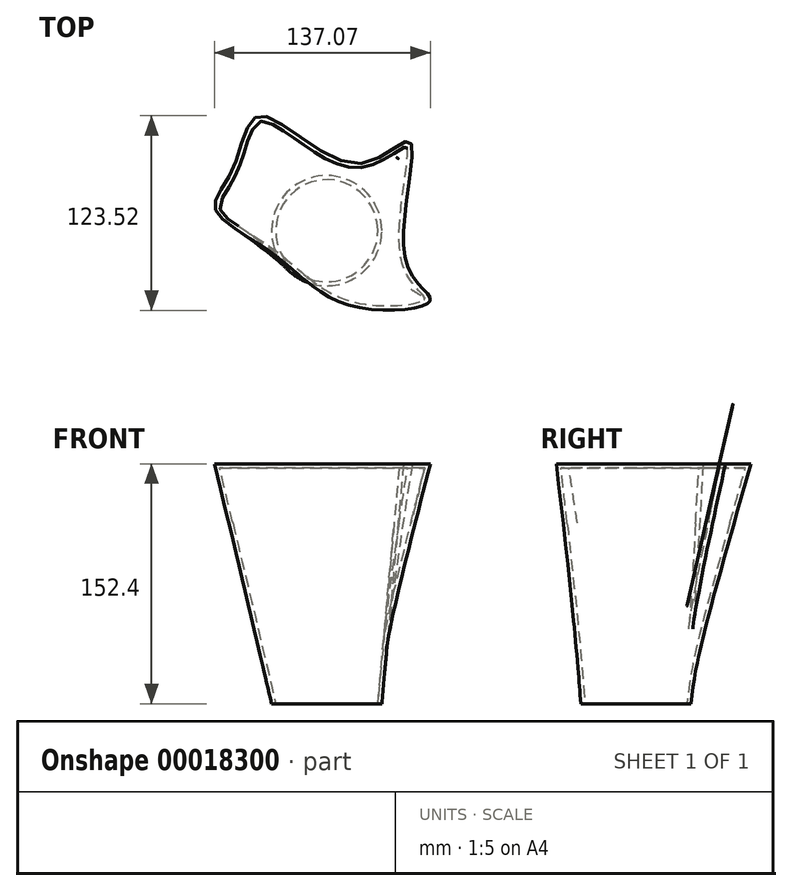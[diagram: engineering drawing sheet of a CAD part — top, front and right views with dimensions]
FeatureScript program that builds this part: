
annotation { "Feature Type Name" : "Feature", "Feature Type Description" : "" }
export const myFeature = defineFeature(function(context is Context, id is Id, definition is map)
    precondition{}
    {
        {
            var Q0;
            Q0=qCreatedBy(makeId("Top.planeOp"),FACE);
            var sketch = newSketch(context, id + "F0", { "sketchPlane" : qUnion([Q0])});
            skCircle(sketch, "E0", {"center": v(0, 0) * mm, "radius": 35.01 * mm});
            skSolve(sketch);
        }
        {
            var Q0;
            Q0=makeQuery(id+"F0.imprint","IMPRINT",FACE,{"disambiguationData":[TD([[makeQuery(id+"F0.imprint","IMPRINT",EDGE,{"derivedFrom":sQuery(id+"F0.wireOp",EDGE,"E0")}),1.0]])]});
            cPlane(context, id + "F1", {"entities" : qUnion([Q0]), "cplaneType" : CPlaneType.OFFSET, "offset" : 152.4 * mm, "width" : 152.4 * mm, "height" : 152.4 * mm});
        }
        {
            var Q0;
            Q0=qCreatedBy(id+"F1.planeOp",FACE);
            var sketch = newSketch(context, id + "F2", { "sketchPlane" : qUnion([Q0])});
            skFitSpline(sketch, "E1", {"points": [v(-59.58, 39.13) * mm, v(-42.4, 72.94) * mm, v(19.08, 42.61) * mm, v(53.06, 56.4) * mm, v(50.65, -20.13) * mm, v(65.68, -44.65) * mm, v(15.92, -47.75) * mm, v(-36.1, -13.13) * mm, v(-70.95, 13.93) * mm, v(-59.58, 39.13) * mm]});
            skSolve(sketch);
        }
        {
            var Q0;
            Q0=makeQuery(id+"F0.imprint","IMPRINT",FACE,{"disambiguationData":[TD([[makeQuery(id+"F0.imprint","IMPRINT",EDGE,{"derivedFrom":sQuery(id+"F0.wireOp",EDGE,"E0")}),1.0]])]});
            var Q1;
            Q1=makeQuery(id+"F2.imprint","IMPRINT",FACE,{"disambiguationData":[TD([[makeQuery(id+"F2.imprint","IMPRINT",EDGE,{"derivedFrom":sQuery(id+"F2.wireOp",EDGE,"E1")}),-1.0]])]});
            loft(context, id + "F3", {"sheetProfilesArray" : [{ "sheetProfileEntities" : qUnion([Q0]) }, { "sheetProfileEntities" : qUnion([Q1]) }]});
        }
        {
            var Q0;
            Q0=makeQuery(id+"F3.opLoft","CAP_FACE",FACE,{"disambiguationData":[OSD([makeQuery(id+"F0.imprint","IMPRINT",FACE,{"disambiguationData":[TD([[makeQuery(id+"F0.imprint","IMPRINT",EDGE,{"derivedFrom":sQuery(id+"F0.wireOp",EDGE,"E0")}),1.0]])]})])],"isStart":true});
            shell(context, id + "F4", {"entities" : qUnion([Q0]), "thickness" : 2.54 * mm});
        }
        {
            var Q0;
            Q0=qCreatedBy(makeId("Front.planeOp"),FACE);
            var sketch = newSketch(context, id + "F5", { "sketchPlane" : qUnion([Q0])});
            skFitSpline(sketch, "E2", {"points": [v(25.8, 40.28) * mm, v(80.61, 32.56) * mm, v(91.66, 96.51) * mm, v(39.37, 128.87) * mm], "startDerivative": vector(195.67, -83.85) * mm, "endDerivative": vector(-195.57, 58.43) * mm});
            skSolve(sketch);
        }
        {
            var Q0;
            Q0=qCreatedBy(makeId("Front.planeOp"),FACE);
            var sketch = newSketch(context, id + "F6", { "sketchPlane" : qUnion([Q0])});
            skFitSpline(sketch, "E3", {"points": [v(-42.3, 48.61) * mm, v(-74.53, 25.8) * mm, v(-94.46, 82.05) * mm, v(-45.26, 120.07) * mm, v(-44.08, 118.35) * mm], "startDerivative": vector(-116.71, -146.42) * mm, "endDerivative": vector(3.5, -37.04) * mm});
            skSolve(sketch);
        }
    });
